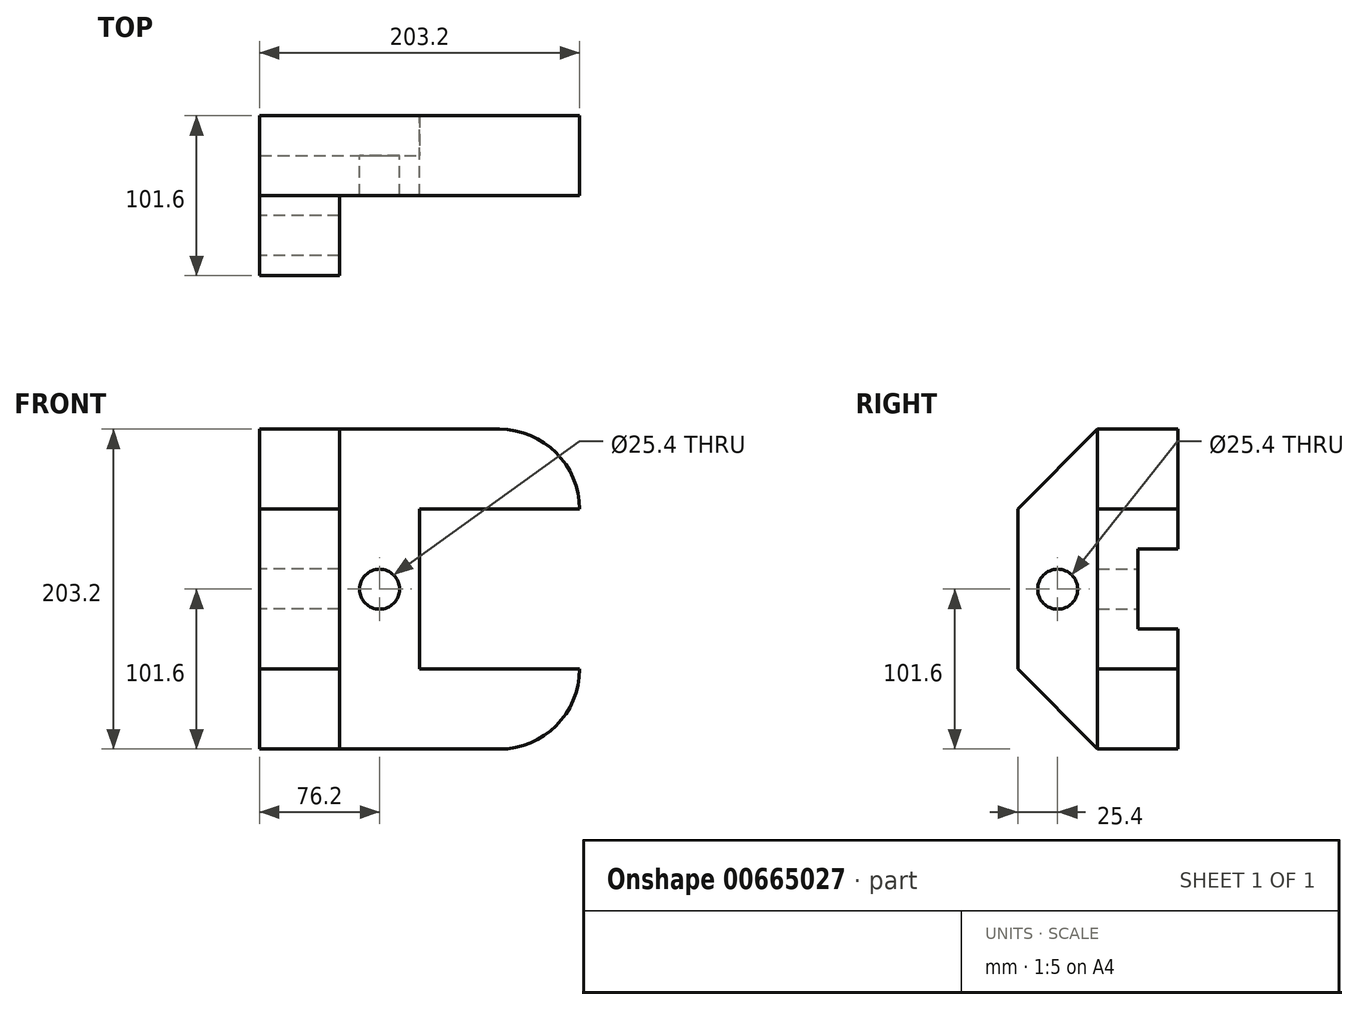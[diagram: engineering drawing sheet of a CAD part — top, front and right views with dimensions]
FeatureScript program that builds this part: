
annotation { "Feature Type Name" : "Feature", "Feature Type Description" : "" }
export const myFeature = defineFeature(function(context is Context, id is Id, definition is map)
    precondition{}
    {
        {
            var Q0;
            Q0=qCreatedBy(makeId("Front.planeOp"),FACE);
            var sketch = newSketch(context, id + "F0", { "sketchPlane" : qUnion([Q0])});
            skLineSegment(sketch, "E0", {"start": v(0, 0) * mm, "end": v(152.4, 0) * mm});
            skLineSegment(sketch, "E1", {"start": v(203.2, 50.8) * mm, "end": v(101.6, 50.8) * mm});
            skLineSegment(sketch, "E2", {"start": v(101.6, 50.8) * mm, "end": v(101.6, 152.4) * mm});
            skLineSegment(sketch, "E3", {"start": v(101.6, 152.4) * mm, "end": v(203.2, 152.4) * mm});
            skLineSegment(sketch, "E4", {"start": v(152.4, 203.2) * mm, "end": v(0, 203.2) * mm});
            skLineSegment(sketch, "E5", {"start": v(0, 203.2) * mm, "end": v(0, 0) * mm});
            skLineSegment(sketch, "E6", {"start": v(203.2, 152.4) * mm, "end": v(152.4, 152.4) * mm});
            skArc(sketch, "E7", {"start": v(203.2, 152.4) * mm, "mid": v(188.32, 188.32) * mm, "end": v(152.4, 203.2) * mm});
            skArc(sketch, "E8", {"start": v(203.2, 50.8) * mm, "mid": v(188.32, 14.88) * mm, "end": v(152.4, 0) * mm});
            skLineSegment(sketch, "E9", {"start": v(101.6, 101.6) * mm, "end": v(50.8, 101.6) * mm});
            skCircle(sketch, "E10", {"center": v(76.2, 101.6) * mm, "radius": 12.7 * mm});
            skSolve(sketch);
        }
        {
            var Q0;
            {var subQ4=sQuery(id+"F0.wireOp",EDGE,"E3");Q0=makeQuery(id+"F0.imprint","IMPRINT",FACE,{"disambiguationData":[TD([[makeQuery(id+"F0.imprint","IMPRINT",EDGE,{"derivedFrom":subQ4}),1.0]])]});}
            var Q1;
            {var subQ1=sQuery(id+"F0.wireOp",EDGE,"E0");Q1=makeQuery(id+"F0.imprint","IMPRINT",FACE,{"disambiguationData":[TD([[makeQuery(id+"F0.imprint","IMPRINT",EDGE,{"derivedFrom":subQ1}),1.0]])]});}
            extrude(context, id + "F1", {"entities" : qUnion([Q0, Q1]), "endBound" : BoundingType.SYMMETRIC, "depth" : 50.8 * mm, "offsetDistance" : 25.4 * mm});
        }
        {
            var Q0;
            Q0=makeQuery(id+"F1.opExtrude","SWEPT_FACE",FACE,{"disambiguationData":[OSD([sQuery(id+"F0.wireOp",EDGE,"E5")])]});
            var sketch = newSketch(context, id + "F2", { "sketchPlane" : qUnion([Q0])});
            skLineSegment(sketch, "E11", {"start": v(76.2, 50.8) * mm, "end": v(25.4, 0) * mm});
            skLineSegment(sketch, "E12", {"start": v(76.2, 50.8) * mm, "end": v(76.2, 152.4) * mm});
            skLineSegment(sketch, "E13", {"start": v(76.2, 152.4) * mm, "end": v(25.4, 203.2) * mm});
            skLineSegment(sketch, "E14", {"start": v(76.2, 101.6) * mm, "end": v(25.4, 101.6) * mm});
            skCircle(sketch, "E15", {"center": v(50.8, 101.6) * mm, "radius": 12.7 * mm});
            skSolve(sketch);
        }
        {
            var Q0;
            {var subQ9=sQuery(id+"F2.wireOp",EDGE,"E11");Q0=makeQuery(id+"F2.imprint","IMPRINT",FACE,{"disambiguationData":[TD([[makeQuery(id+"F2.imprint","IMPRINT",EDGE,{"derivedFrom":subQ9}),-1.0]])]});}
            var Q1;
            {var subQ9=sQuery(id+"F2.wireOp",EDGE,"E13");Q1=makeQuery(id+"F2.imprint","IMPRINT",FACE,{"disambiguationData":[TD([[makeQuery(id+"F2.imprint","IMPRINT",EDGE,{"derivedFrom":subQ9}),1.0]])]});}
            extrude(context, id + "F3", {"entities" : qUnion([Q0, Q1]), "operationType" : NewBodyOperationType.ADD, "oppositeDirection" : true, "depth" : 50.8 * mm, "offsetDistance" : 25.4 * mm});
        }
        {
            var Q0;
            Q0=makeQuery(id+"F1.opExtrude","SWEPT_FACE",FACE,{"disambiguationData":[OSD([sQuery(id+"F0.wireOp",EDGE,"E2")])]});
            var sketch = newSketch(context, id + "F4", { "sketchPlane" : qUnion([Q0])});
            skLineSegment(sketch, "E16", {"start": v(25.4, 152.4) * mm, "end": v(25.4, 127) * mm});
            skLineSegment(sketch, "E17", {"start": v(25.4, 127) * mm, "end": v(0, 127) * mm});
            skLineSegment(sketch, "E18", {"start": v(0, 127) * mm, "end": v(0, 76.2) * mm});
            skLineSegment(sketch, "E19", {"start": v(0, 76.2) * mm, "end": v(25.4, 76.2) * mm});
            skSolve(sketch);
        }
        {
            var Q0;
            {var subQ0=sQuery(id+"F4.wireOp",EDGE,"E17");Q0=makeQuery(id+"F4.imprint","IMPRINT",FACE,{"disambiguationData":[TD([[makeQuery(id+"F4.imprint","IMPRINT",EDGE,{"derivedFrom":subQ0}),1.0]])]});}
            extrude(context, id + "F5", {"entities" : qUnion([Q0]), "operationType" : NewBodyOperationType.REMOVE, "oppositeDirection" : true, "depth" : 101.6 * mm, "offsetDistance" : 25.4 * mm});
        }
    });
